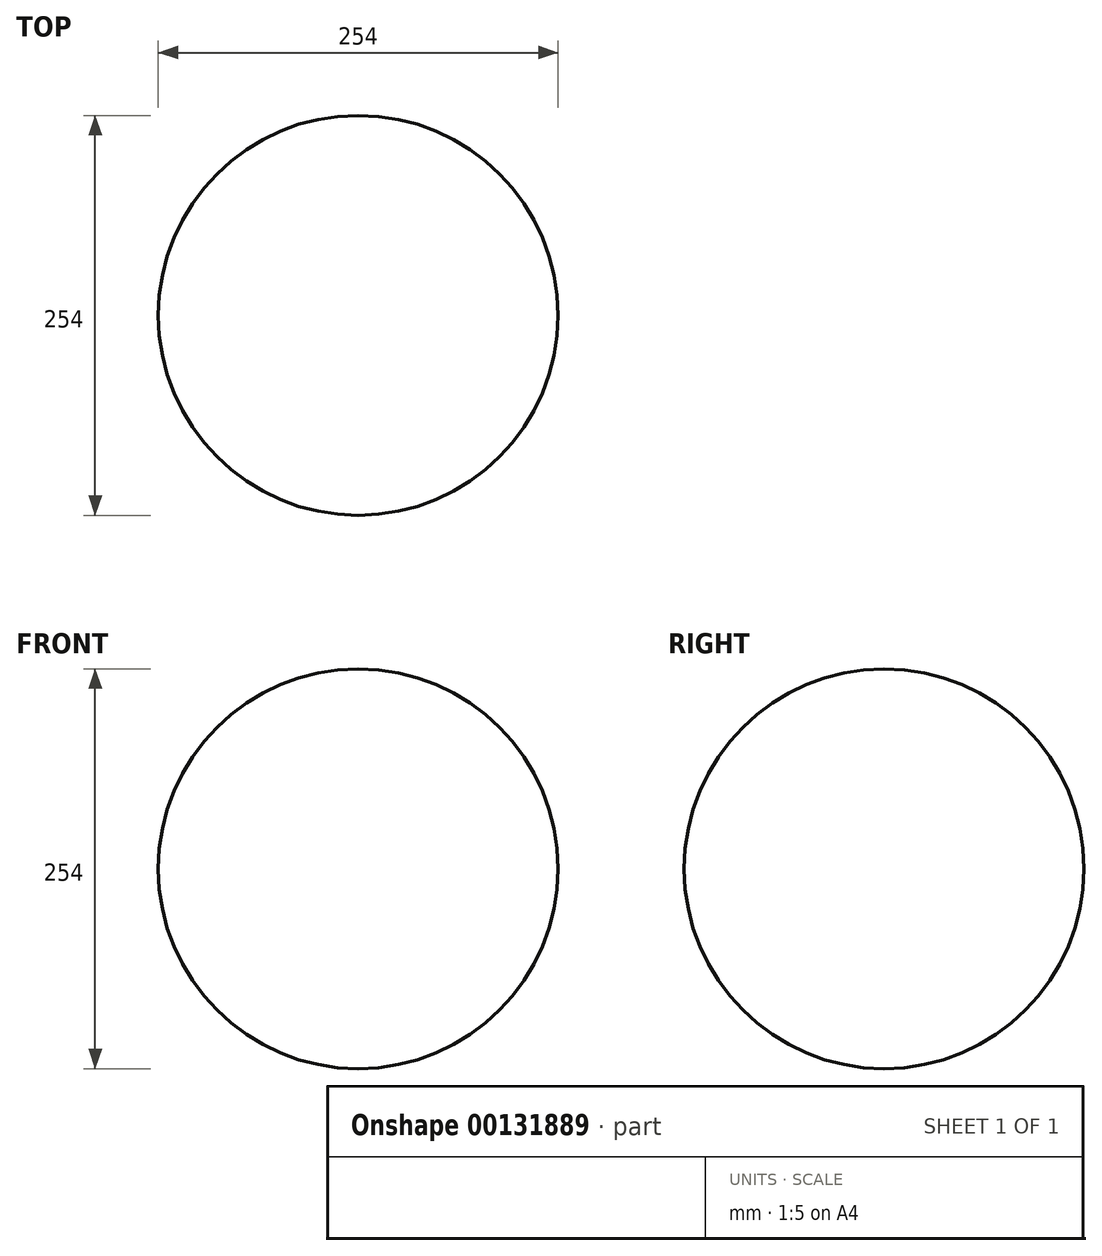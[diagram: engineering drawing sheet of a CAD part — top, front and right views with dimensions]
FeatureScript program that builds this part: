
annotation { "Feature Type Name" : "Feature", "Feature Type Description" : "" }
export const myFeature = defineFeature(function(context is Context, id is Id, definition is map)
    precondition{}
    {
        {
            var Q0;
            Q0=qCreatedBy(makeId("Front.planeOp"),FACE);
            var sketch = newSketch(context, id + "F0", { "sketchPlane" : qUnion([Q0])});
            skArc(sketch, "E0", {"start": v(127, 0) * mm, "mid": v(0, 127) * mm, "end": v(-127, 0) * mm});
            skLineSegment(sketch, "E1", {"start": v(-127, 0) * mm, "end": v(127, 0) * mm});
            skSolve(sketch);
        }
        {
            var Q0;
            Q0 = qSketchRegion(id + "F0", true);
            var Q1;
            Q1=sQuery(id+"F0.wireOp",EDGE,"E1");
            revolve(context, id + "F1", {"entities" : qUnion([Q0]), "axis" : qUnion([Q1]), "revolveType" : RevolveType.FULL});
        }
    });
